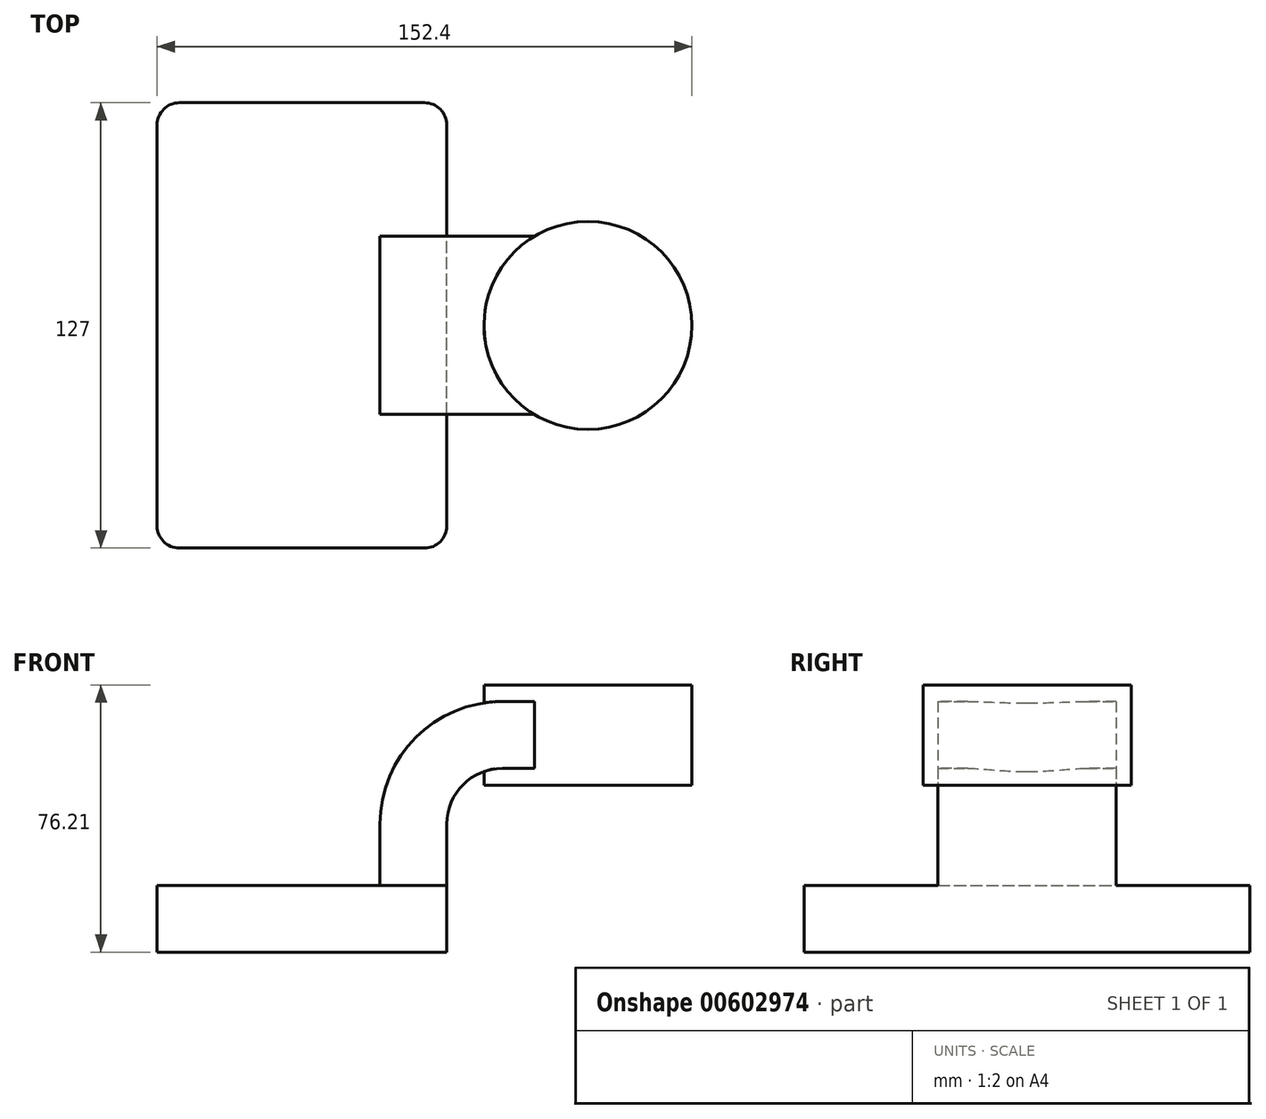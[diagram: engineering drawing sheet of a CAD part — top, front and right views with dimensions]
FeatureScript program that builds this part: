
annotation { "Feature Type Name" : "Feature", "Feature Type Description" : "" }
export const myFeature = defineFeature(function(context is Context, id is Id, definition is map)
    precondition{}
    {
        {
            var Q0;
            Q0=qCreatedBy(makeId("Front.planeOp"),FACE);
            var sketch = newSketch(context, id + "F0", { "sketchPlane" : qUnion([Q0])});
            skLineSegment(sketch, "E0.bottom", {"start": v(41.28, -9.52) * mm, "end": v(-41.27, -9.52) * mm});
            skLineSegment(sketch, "E0.top", {"start": v(41.27, 9.53) * mm, "end": v(-41.28, 9.53) * mm});
            skLineSegment(sketch, "E0.left", {"start": v(41.28, -9.52) * mm, "end": v(41.28, 9.53) * mm});
            skLineSegment(sketch, "E0.right", {"start": v(-41.28, -9.52) * mm, "end": v(-41.28, 9.53) * mm});
            skPoint(sketch, "E0.middle", {"position": v(0, 0) * mm});
            skLineSegment(sketch, "E1.bottom", {"start": v(60.33, 38.1) * mm, "end": v(111.12, 38.1) * mm});
            skLineSegment(sketch, "E1.top", {"start": v(60.32, 66.68) * mm, "end": v(111.12, 66.68) * mm});
            skLineSegment(sketch, "E1.left", {"start": v(60.33, 38.1) * mm, "end": v(60.32, 66.68) * mm});
            skLineSegment(sketch, "E1.right", {"start": v(111.13, 38.1) * mm, "end": v(111.12, 66.68) * mm});
            skPoint(sketch, "E1.middle", {"position": v(85.72, 52.39) * mm});
            skLineSegment(sketch, "E2", {"start": v(41.27, 9.53) * mm, "end": v(41.27, 27) * mm});
            skArc(sketch, "E3", {"start": v(41.27, 27) * mm, "mid": v(45.92, 38.23) * mm, "end": v(57.15, 42.88) * mm});
            skLineSegment(sketch, "E4", {"start": v(57.15, 42.88) * mm, "end": v(81.49, 42.88) * mm});
            skLineSegment(sketch, "E5.0", {"start": v(57.15, 61.93) * mm, "end": v(81.49, 61.93) * mm});
            skArc(sketch, "E5.1", {"start": v(22.22, 27) * mm, "mid": v(32.45, 51.7) * mm, "end": v(57.15, 61.93) * mm});
            skLineSegment(sketch, "E5.2", {"start": v(22.22, 9.53) * mm, "end": v(22.22, 27) * mm});
            skLineSegment(sketch, "E6", {"start": v(81.49, 38.1) * mm, "end": v(81.49, 66.68) * mm});
            skFitSpline(sketch, "E7", {"points": [v(-41.28, 9.52) * mm, v(57.15, 61.93) * mm], "startDerivative": vector(0, 121.65) * mm, "endDerivative": vector(112.5, 0) * mm});
            skSolve(sketch);
        }
        {
            var Q0;
            Q0=makeQuery(id+"F0.imprint","IMPRINT",FACE,{"disambiguationData":[TD([[makeQuery(id+"F0.imprint","IMPRINT",EDGE,{"derivedFrom":sQuery(id+"F0.wireOp",EDGE,"E0.bottom")}),-1.0]])]});
            extrude(context, id + "F1", {"entities" : qUnion([Q0]), "endBound" : BoundingType.SYMMETRIC, "depth" : 127 * mm, "offsetDistance" : 25.4 * mm});
        }
        {
            var Q0;
            {var subQ1=sQuery(id+"F0.wireOp",EDGE,"E2");Q0=makeQuery(id+"F0.imprint","IMPRINT",FACE,{"disambiguationData":[TD([[makeQuery(id+"F0.imprint","IMPRINT",EDGE,{"derivedFrom":subQ1}),1.0]])]});}
            var Q1;
            {var subQ0=sQuery(id+"F0.wireOp",EDGE,"E4");var subQ1=sQuery(id+"F0.wireOp",EDGE,"E1.left");var subQ2=makeQuery(id+"F0.imprint","INTERSECT",VERTEX,{"derivedFrom":[subQ1,subQ0]});Q1=makeQuery(id+"F0.imprint","IMPRINT",FACE,{"disambiguationData":[TD([[makeQuery(id+"F0.imprint","IMPRINT",EDGE,{"disambiguationData":[TD([[subQ2,-1.0]])],"derivedFrom":subQ1}),-1.0]])]});}
            extrude(context, id + "F2", {"entities" : qUnion([Q0, Q1]), "operationType" : NewBodyOperationType.ADD, "endBound" : BoundingType.SYMMETRIC, "depth" : 50.8 * mm, "offsetDistance" : 25.4 * mm});
        }
        {
            var Q0;
            Q0=makeQuery(id+"F0.imprint","IMPRINT",FACE,{"disambiguationData":[TD([[makeQuery(id+"F0.imprint","IMPRINT",EDGE,{"derivedFrom":sQuery(id+"F0.wireOp",EDGE,"E5.1")}),1.0]])]});
            extrude(context, id + "F3", {"entities" : qUnion([Q0]), "operationType" : NewBodyOperationType.ADD, "endBound" : BoundingType.SYMMETRIC, "depth" : 15.88 * mm, "offsetDistance" : 25.4 * mm});
        }
        {
            var Q0;
            {var subQ0=sQuery(id+"F0.wireOp",EDGE,"E1.right");Q0=makeQuery(id+"F0.imprint","IMPRINT",FACE,{"disambiguationData":[TD([[makeQuery(id+"F0.imprint","IMPRINT",EDGE,{"derivedFrom":subQ0}),1.0]])]});}
            var Q1;
            Q1=sQuery(id+"F0.wireOp",EDGE,"E6");
            revolve(context, id + "F4", {"operationType" : NewBodyOperationType.ADD, "entities" : qUnion([Q0]), "axis" : qUnion([Q1]), "revolveType" : RevolveType.FULL});
        }
        {
            var Q0;
            Q0=makeQuery(id+"F1.opExtrude","CAP_EDGE",EDGE,{"disambiguationData":[OSD([sQuery(id+"F0.wireOp",EDGE,"E0.right")])],"isStart":true});
            var Q1;
            Q1=makeQuery(id+"F1.opExtrude","CAP_EDGE",EDGE,{"disambiguationData":[OSD([sQuery(id+"F0.wireOp",EDGE,"E0.right")])],"isStart":false});
            var Q2;
            Q2=makeQuery(id+"F1.opExtrude","CAP_EDGE",EDGE,{"disambiguationData":[OSD([sQuery(id+"F0.wireOp",EDGE,"E0.left")])],"isStart":false});
            var Q3;
            Q3=makeQuery(id+"F1.opExtrude","CAP_EDGE",EDGE,{"disambiguationData":[OSD([sQuery(id+"F0.wireOp",EDGE,"E0.left")])],"isStart":true});
            fillet(context, id + "F5", {"entities" : qUnion([Q0, Q1, Q2, Q3]), "radius" : 6.35 * mm, "tangentPropagation" : true, "allowEdgeOverflow" : false});
        }
    });
